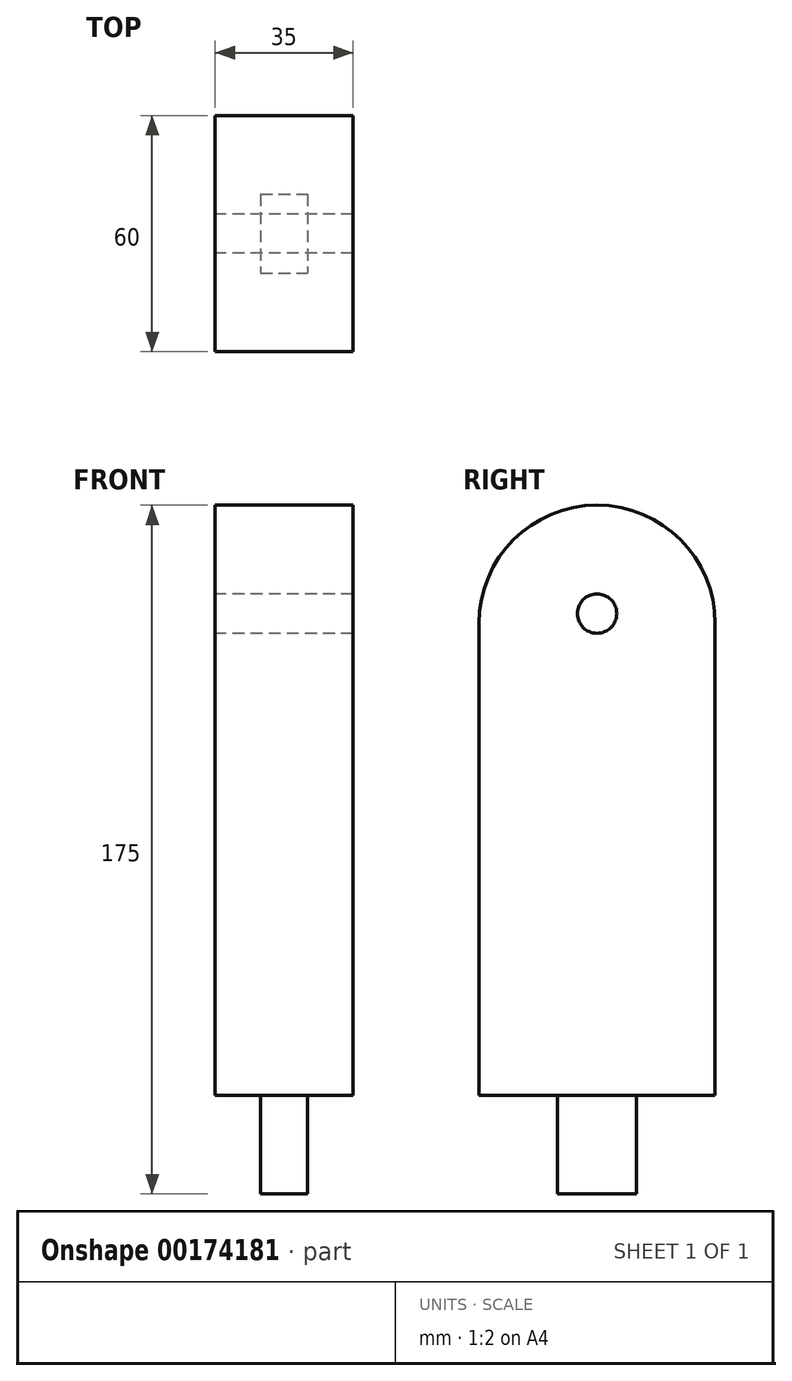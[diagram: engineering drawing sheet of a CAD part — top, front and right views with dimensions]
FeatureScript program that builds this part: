
annotation { "Feature Type Name" : "Feature", "Feature Type Description" : "" }
export const myFeature = defineFeature(function(context is Context, id is Id, definition is map)
    precondition{}
    {
        {
            var Q0;
            Q0=qCreatedBy(makeId("Top.planeOp"),FACE);
            var sketch = newSketch(context, id + "F0", { "sketchPlane" : qUnion([Q0])});
            skLineSegment(sketch, "E0.bottom", {"start": v(-17.5, 30) * mm, "end": v(17.5, 30) * mm});
            skLineSegment(sketch, "E0.top", {"start": v(-17.5, -30) * mm, "end": v(17.5, -30) * mm});
            skLineSegment(sketch, "E0.left", {"start": v(-17.5, 30) * mm, "end": v(-17.5, -30) * mm});
            skLineSegment(sketch, "E0.right", {"start": v(17.5, 30) * mm, "end": v(17.5, -30) * mm});
            skSolve(sketch);
        }
        {
            var Q0;
            Q0=makeQuery(id+"F0.imprint","IMPRINT",FACE,{"disambiguationData":[TD([[makeQuery(id+"F0.imprint","IMPRINT",EDGE,{"derivedFrom":sQuery(id+"F0.wireOp",EDGE,"E0.bottom")}),-1.0]])]});
            extrude(context, id + "F1", {"entities" : qUnion([Q0]), "depth" : 150 * mm});
        }
        {
            var Q0;
            Q0=makeQuery(id+"F1.opExtrude","CAP_FACE",FACE,{"disambiguationData":[OSD([sQuery(id+"F0.wireOp",EDGE,"E0.bottom"),sQuery(id+"F0.wireOp",EDGE,"E0.top"),sQuery(id+"F0.wireOp",EDGE,"E0.left"),sQuery(id+"F0.wireOp",EDGE,"E0.right")])],"isStart":true});
            var sketch = newSketch(context, id + "F2", { "sketchPlane" : qUnion([Q0])});
            skLineSegment(sketch, "E1.bottom", {"start": v(-6, -10) * mm, "end": v(6, -10) * mm});
            skLineSegment(sketch, "E1.top", {"start": v(-6, 10) * mm, "end": v(6, 10) * mm});
            skLineSegment(sketch, "E1.left", {"start": v(-6, -10) * mm, "end": v(-6, 10) * mm});
            skLineSegment(sketch, "E1.right", {"start": v(6, -10) * mm, "end": v(6, 10) * mm});
            skSolve(sketch);
        }
        {
            var Q0;
            Q0=makeQuery(id+"F2.imprint","IMPRINT",FACE,{"disambiguationData":[TD([[makeQuery(id+"F2.imprint","IMPRINT",EDGE,{"derivedFrom":sQuery(id+"F2.wireOp",EDGE,"E1.bottom")}),1.0]])]});
            extrude(context, id + "F3", {"entities" : qUnion([Q0]), "operationType" : NewBodyOperationType.ADD, "depth" : 25 * mm});
        }
        {
            var Q0;
            Q0=makeQuery(id+"F1.opExtrude","CAP_EDGE",EDGE,{"disambiguationData":[OSD([sQuery(id+"F0.wireOp",EDGE,"E0.top")])],"isStart":false});
            var Q1;
            Q1=makeQuery(id+"F1.opExtrude","CAP_EDGE",EDGE,{"disambiguationData":[OSD([sQuery(id+"F0.wireOp",EDGE,"E0.bottom")])],"isStart":false});
            fillet(context, id + "F4", {"entities" : qUnion([Q0, Q1]), "radius" : 30 * mm, "tangentPropagation" : true, "allowEdgeOverflow" : false});
        }
        {
            var Q0;
            Q0=makeQuery(id+"F1.opExtrude","SWEPT_FACE",FACE,{"disambiguationData":[OSD([sQuery(id+"F0.wireOp",EDGE,"E0.left")])]});
            var sketch = newSketch(context, id + "F5", { "sketchPlane" : qUnion([Q0])});
            skLineSegment(sketch, "E2", {"start": v(0, 0) * mm, "end": v(0, 150) * mm, "construction": true});
            skLineSegment(sketch, "E3", {"start": v(-29.9, 122.46) * mm, "end": v(30, 122.46) * mm, "construction": true});
            skCircle(sketch, "E4", {"center": v(0, 122.46) * mm, "radius": 5 * mm});
            skSolve(sketch);
        }
        {
            var Q0;
            Q0=sQuery(id+"F5.wireOp",VERTEX,"E4.center");
            var Q1;
            Q1=makeQuery(id+"F1.opExtrude","SWEPT_BODY",BODY,{"disambiguationData":[OSD([sQuery(id+"F0.wireOp",EDGE,"E0.bottom"),sQuery(id+"F0.wireOp",EDGE,"E0.top"),sQuery(id+"F0.wireOp",EDGE,"E0.left"),sQuery(id+"F0.wireOp",EDGE,"E0.right")])]});
            hole(context, id + "F6", {"style" : HoleStyle.SIMPLE, "endStyle" : HoleEndStyle.THROUGH, "holeDiameter" : 10 * mm, "locations" : qUnion([Q0]), "scope" : qUnion([Q1]), "isTappedThrough" : true});
        }
    });
